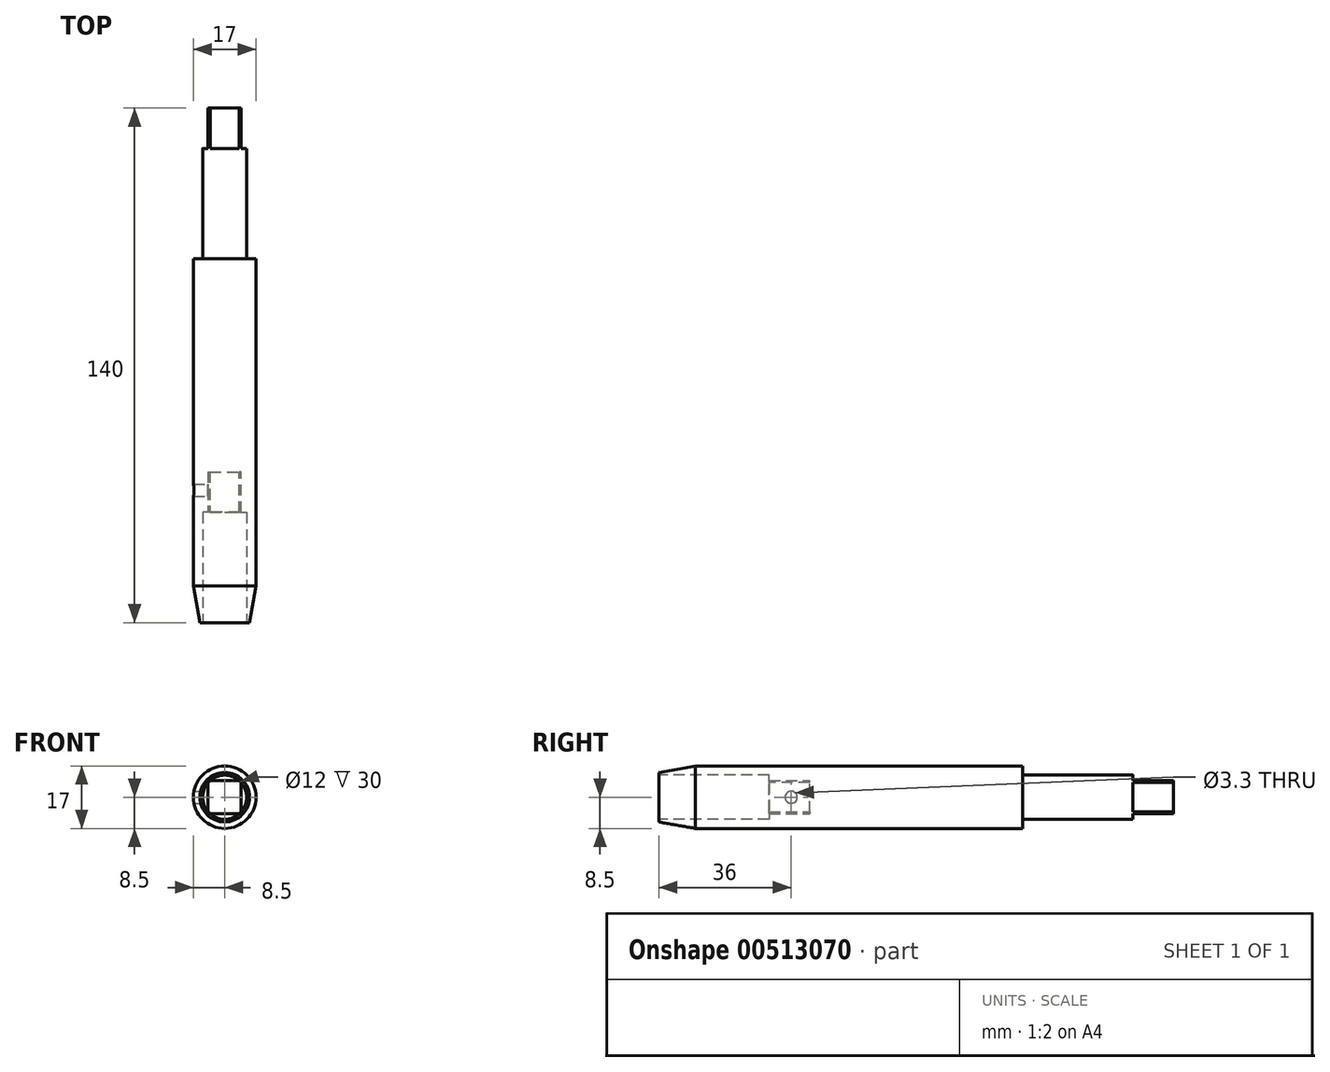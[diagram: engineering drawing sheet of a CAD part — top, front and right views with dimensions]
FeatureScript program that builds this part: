
annotation { "Feature Type Name" : "Feature", "Feature Type Description" : "" }
export const myFeature = defineFeature(function(context is Context, id is Id, definition is map)
    precondition{}
    {
        {
            var Q0;
            Q0=qCreatedBy(makeId("Front.planeOp"),FACE);
            var sketch = newSketch(context, id + "F0", { "sketchPlane" : qUnion([Q0])});
            skCircle(sketch, "E0", {"center": v(0, 0) * mm, "radius": 8.5 * mm});
            skSolve(sketch);
        }
        {
            var Q0;
            Q0 = qSketchRegion(id + "F0", true);
            extrude(context, id + "F1", {"entities" : qUnion([Q0]), "depth" : 140 * mm});
        }
        {
            var Q0;
            Q0=makeQuery(id+"F1.opExtrude","CAP_FACE",FACE,{"disambiguationData":[OSD([sQuery(id+"F0.wireOp",EDGE,"E0")])],"isStart":false});
            var sketch = newSketch(context, id + "F2", { "sketchPlane" : qUnion([Q0])});
            skCircle(sketch, "E1", {"center": v(0, 0) * mm, "radius": 6 * mm});
            skSolve(sketch);
        }
        {
            var Q0;
            Q0 = qSketchRegion(id + "F2", true);
            extrude(context, id + "F3", {"entities" : qUnion([Q0]), "operationType" : NewBodyOperationType.REMOVE, "oppositeDirection" : true, "depth" : 30 * mm});
        }
        {
            var Q0;
            Q0=makeQuery(id+"F3.boolean.opBoolean","COPY",FACE,{"derivedFrom":makeQuery(id+"F3.opExtrude","CAP_FACE",FACE,{"disambiguationData":[OSD([sQuery(id+"F2.wireOp",EDGE,"E1")])],"isStart":false})});
            var sketch = newSketch(context, id + "F4", { "sketchPlane" : qUnion([Q0])});
            skLineSegment(sketch, "E2.bottom", {"start": v(-4.5, -4.5) * mm, "end": v(4.5, -4.5) * mm});
            skLineSegment(sketch, "E2.top", {"start": v(-4.5, 4.5) * mm, "end": v(4.5, 4.5) * mm});
            skLineSegment(sketch, "E2.left", {"start": v(-4.5, -4.5) * mm, "end": v(-4.5, 4.5) * mm});
            skLineSegment(sketch, "E2.right", {"start": v(4.5, -4.5) * mm, "end": v(4.5, 4.5) * mm});
            skPoint(sketch, "E2.middle", {"position": v(0, 0) * mm});
            skSolve(sketch);
        }
        {
            var Q0;
            Q0 = qSketchRegion(id + "F4", true);
            extrude(context, id + "F5", {"entities" : qUnion([Q0]), "operationType" : NewBodyOperationType.REMOVE, "oppositeDirection" : true, "depth" : 11 * mm});
        }
        {
            var Q0;
            Q0=makeQuery(id+"F5.boolean.opBoolean","COPY",EDGE,{"derivedFrom":makeQuery(id+"F5.opExtrude","SWEPT_EDGE",EDGE,{"disambiguationData":[OSD([sQuery(id+"F4.wireOp",EDGE,"E2.bottom"),sQuery(id+"F4.wireOp",EDGE,"E2.left")])]})});
            chamfer(context, id + "F6", {"entities" : qUnion([Q0]), "width" : .5 * mm, "tangentPropagation" : true});
        }
        {
            var Q0;
            Q0=makeQuery(id+"F5.boolean.opBoolean","COPY",EDGE,{"derivedFrom":makeQuery(id+"F5.opExtrude","SWEPT_EDGE",EDGE,{"disambiguationData":[OSD([sQuery(id+"F4.wireOp",EDGE,"E2.bottom"),sQuery(id+"F4.wireOp",EDGE,"E2.right")])]})});
            chamfer(context, id + "F7", {"entities" : qUnion([Q0]), "width" : .5 * mm, "tangentPropagation" : true});
        }
        {
            var Q0;
            Q0=makeQuery(id+"F5.boolean.opBoolean","COPY",EDGE,{"derivedFrom":makeQuery(id+"F5.opExtrude","SWEPT_EDGE",EDGE,{"disambiguationData":[OSD([sQuery(id+"F4.wireOp",EDGE,"E2.top"),sQuery(id+"F4.wireOp",EDGE,"E2.right")])]})});
            var Q1;
            Q1=makeQuery(id+"F5.boolean.opBoolean","COPY",EDGE,{"derivedFrom":makeQuery(id+"F5.opExtrude","SWEPT_EDGE",EDGE,{"disambiguationData":[OSD([sQuery(id+"F4.wireOp",EDGE,"E2.top"),sQuery(id+"F4.wireOp",EDGE,"E2.left")])]})});
            chamfer(context, id + "F8", {"entities" : qUnion([Q0, Q1]), "width" : .5 * mm, "tangentPropagation" : true});
        }
        {
            var Q0;
            Q0=makeQuery(id+"F5.boolean.opBoolean","COPY",FACE,{"derivedFrom":makeQuery(id+"F5.opExtrude","SWEPT_FACE",FACE,{"disambiguationData":[OSD([sQuery(id+"F4.wireOp",EDGE,"E2.left")])]})});
            var sketch = newSketch(context, id + "F9", { "sketchPlane" : qUnion([Q0])});
            skCircle(sketch, "E3", {"center": v(-104, 0) * mm, "radius": 1.65 * mm});
            skSolve(sketch);
        }
        {
            var Q0;
            Q0 = qSketchRegion(id + "F9", true);
            extrude(context, id + "F10", {"entities" : qUnion([Q0]), "operationType" : NewBodyOperationType.REMOVE, "oppositeDirection" : true, "depth" : 25 * mm});
        }
        {
            var Q0;
            Q0=makeQuery(id+"F1.opExtrude","CAP_FACE",FACE,{"disambiguationData":[OSD([sQuery(id+"F0.wireOp",EDGE,"E0")])],"isStart":true});
            var sketch = newSketch(context, id + "F11", { "sketchPlane" : qUnion([Q0])});
            skCircle(sketch, "E4", {"center": v(0, 0) * mm, "radius": 6 * mm});
            skSolve(sketch);
        }
        {
            var Q0;
            Q0=makeQuery(id+"F11.imprint","IMPRINT",FACE,{"disambiguationData":[TD([[makeQuery(id+"F11.imprint","IMPRINT",EDGE,{"derivedFrom":sQuery(id+"F11.wireOp",EDGE,"E4")}),-1.0]])]});
            extrude(context, id + "F12", {"entities" : qUnion([Q0]), "operationType" : NewBodyOperationType.REMOVE, "oppositeDirection" : true, "depth" : 41 * mm});
        }
        {
            var Q0;
            Q0=makeQuery(id+"F1.opExtrude","CAP_FACE",FACE,{"disambiguationData":[OSD([sQuery(id+"F0.wireOp",EDGE,"E0")])],"isStart":true});
            var sketch = newSketch(context, id + "F13", { "sketchPlane" : qUnion([Q0])});
            skLineSegment(sketch, "E5.bottom", {"start": v(-4.5, -4.5) * mm, "end": v(4.5, -4.5) * mm});
            skLineSegment(sketch, "E5.top", {"start": v(-4.5, 4.5) * mm, "end": v(4.5, 4.5) * mm});
            skLineSegment(sketch, "E5.left", {"start": v(-4.5, -4.5) * mm, "end": v(-4.5, 4.5) * mm});
            skLineSegment(sketch, "E5.right", {"start": v(4.5, -4.5) * mm, "end": v(4.5, 4.5) * mm});
            skPoint(sketch, "E5.middle", {"position": v(0, 0) * mm});
            skSolve(sketch);
        }
        {
            var Q0;
            {var subQ0=sQuery(id+"F13.wireOp",EDGE,"E5.top");var subQ1=makeQuery(id+"F12.boolean.opBoolean","COPY",EDGE,{"derivedFrom":makeQuery(id+"F12.opExtrude","CAP_EDGE",EDGE,{"disambiguationData":[OSD([sQuery(id+"F11.wireOp",EDGE,"E4")])],"isStart":true})});var subQ2=makeQuery(id+"F13.imprint","INTERSECT",VERTEX,{"disambiguationData":[OD(0.0)],"derivedFrom":[subQ1,subQ0]});Q0=makeQuery(id+"F13.imprint","IMPRINT",FACE,{"disambiguationData":[TD([[makeQuery(id+"F13.imprint","IMPRINT",EDGE,{"disambiguationData":[TD([[subQ2,-1.0]])],"derivedFrom":subQ0}),1.0]])]});}
            var Q1;
            {var subQ0=sQuery(id+"F13.wireOp",EDGE,"E5.right");var subQ1=makeQuery(id+"F12.boolean.opBoolean","COPY",EDGE,{"derivedFrom":makeQuery(id+"F12.opExtrude","CAP_EDGE",EDGE,{"disambiguationData":[OSD([sQuery(id+"F11.wireOp",EDGE,"E4")])],"isStart":true})});var subQ2=makeQuery(id+"F13.imprint","INTERSECT",VERTEX,{"disambiguationData":[OD(0.0)],"derivedFrom":[subQ1,subQ0]});Q1=makeQuery(id+"F13.imprint","IMPRINT",FACE,{"disambiguationData":[TD([[makeQuery(id+"F13.imprint","IMPRINT",EDGE,{"disambiguationData":[TD([[subQ2,-1.0]])],"derivedFrom":subQ0}),-1.0]])]});}
            var Q2;
            {var subQ0=sQuery(id+"F13.wireOp",EDGE,"E5.bottom");var subQ1=makeQuery(id+"F12.boolean.opBoolean","COPY",EDGE,{"derivedFrom":makeQuery(id+"F12.opExtrude","CAP_EDGE",EDGE,{"disambiguationData":[OSD([sQuery(id+"F11.wireOp",EDGE,"E4")])],"isStart":true})});var subQ2=makeQuery(id+"F13.imprint","INTERSECT",VERTEX,{"disambiguationData":[OD(0.0)],"derivedFrom":[subQ1,subQ0]});Q2=makeQuery(id+"F13.imprint","IMPRINT",FACE,{"disambiguationData":[TD([[makeQuery(id+"F13.imprint","IMPRINT",EDGE,{"disambiguationData":[TD([[subQ2,-1.0]])],"derivedFrom":subQ0}),-1.0]])]});}
            var Q3;
            {var subQ0=sQuery(id+"F13.wireOp",EDGE,"E5.left");var subQ1=makeQuery(id+"F12.boolean.opBoolean","COPY",EDGE,{"derivedFrom":makeQuery(id+"F12.opExtrude","CAP_EDGE",EDGE,{"disambiguationData":[OSD([sQuery(id+"F11.wireOp",EDGE,"E4")])],"isStart":true})});var subQ2=makeQuery(id+"F13.imprint","INTERSECT",VERTEX,{"disambiguationData":[OD(0.0)],"derivedFrom":[subQ1,subQ0]});Q3=makeQuery(id+"F13.imprint","IMPRINT",FACE,{"disambiguationData":[TD([[makeQuery(id+"F13.imprint","IMPRINT",EDGE,{"disambiguationData":[TD([[subQ2,-1.0]])],"derivedFrom":subQ0}),1.0]])]});}
            extrude(context, id + "F14", {"entities" : qUnion([Q0, Q1, Q2, Q3]), "operationType" : NewBodyOperationType.REMOVE, "oppositeDirection" : true, "depth" : 11 * mm});
        }
        {
            var Q0;
            Q0=makeQuery(id+"F1.opExtrude","CAP_EDGE",EDGE,{"disambiguationData":[OSD([sQuery(id+"F0.wireOp",EDGE,"E0")])],"isStart":false});
            chamfer(context, id + "F15", {"entities" : qUnion([Q0]), "chamferType" : ChamferType.OFFSET_ANGLE, "width" : 10 * mm, "oppositeDirection" : true, "angle" : 10 * degree, "tangentPropagation" : true});
        }
    });
